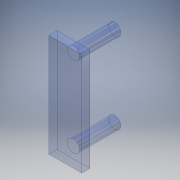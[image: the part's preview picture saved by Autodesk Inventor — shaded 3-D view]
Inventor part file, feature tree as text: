
AUTODESK INVENTOR PART (.ipt)
format: ipt  version: 2018 (Build 220112000, 112)  size: 110,592 bytes
history: native  units: mm
features: extrude x2, sketch x1
ambient origin geometry x8: Origin, YZ Plane, XZ Plane, XY Plane, X Axis, Y Axis, Z Axis, Center Point
bodies: 实体1 (feature_tree)
feature tree (3):
  sketch  "草图1"  dims[d0=25.0mm d1=8.0mm d2=3.0mm d6=19.57mm d7=10.0mm d8=0.0mm d9=2.0mm d10=0.0mm]
  extrude  "拉伸1"  Depth=8.0mm
  extrude  "拉伸2"  Depth=2.0mm
